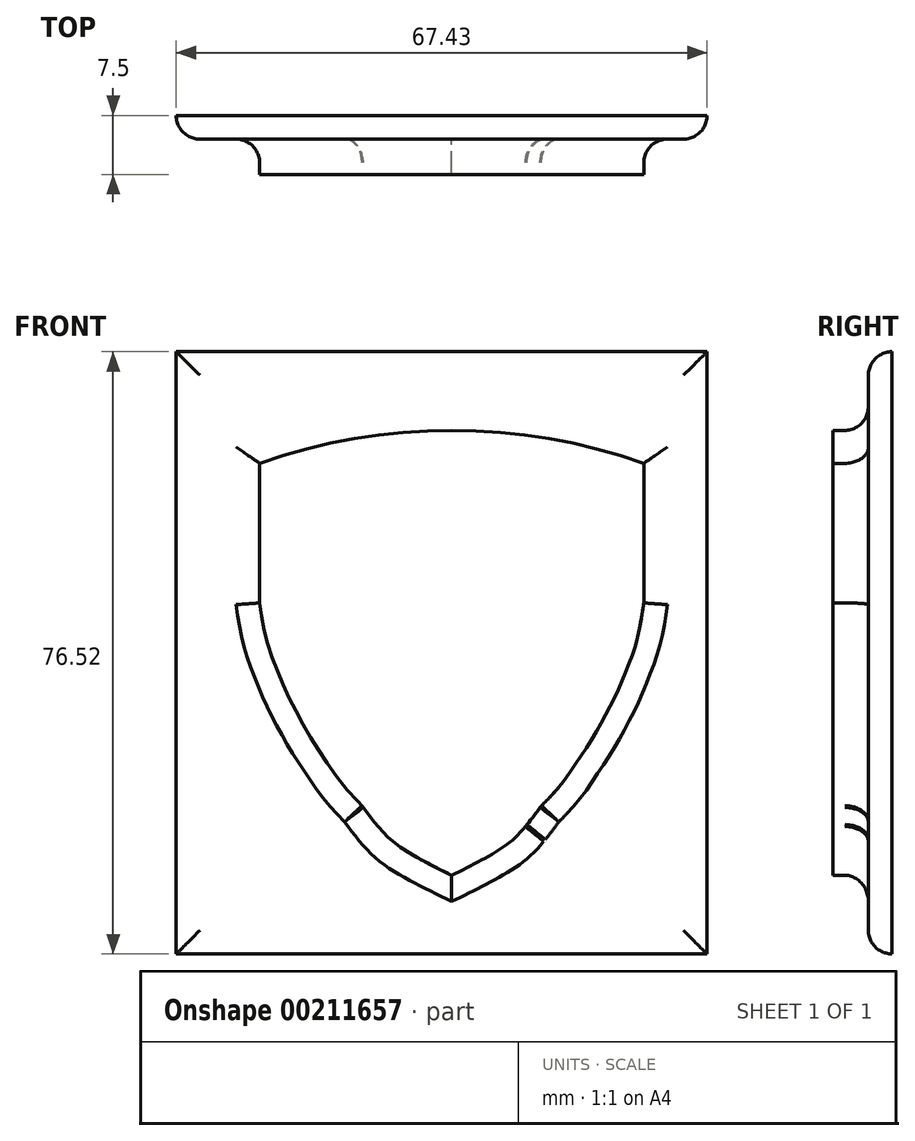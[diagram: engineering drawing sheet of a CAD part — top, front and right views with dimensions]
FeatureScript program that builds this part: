
annotation { "Feature Type Name" : "Feature", "Feature Type Description" : "" }
export const myFeature = defineFeature(function(context is Context, id is Id, definition is map)
    precondition{}
    {
        {
            var Q0;
            Q0=qCreatedBy(makeId("Front.planeOp"),FACE);
            var sketch = newSketch(context, id + "F0", { "sketchPlane" : qUnion([Q0])});
            skLineSegment(sketch, "E0", {"start": v(0, 9.74) * mm, "end": v(0, -11.29) * mm, "construction": true});
            skPoint(sketch, "E1", {"position": v(0, 0) * mm});
            skPoint(sketch, "E2", {"position": v(5.18, 2.71) * mm});
            skPoint(sketch, "E3", {"position": v(8.7, 5.42) * mm});
            skPoint(sketch, "E4", {"position": v(11.31, 8.72) * mm});
            skPoint(sketch, "E5", {"position": v(13.8, 11.44) * mm});
            skPoint(sketch, "E6", {"position": v(16.12, 14.74) * mm});
            skPoint(sketch, "E7", {"position": v(17.92, 17.5) * mm});
            skPoint(sketch, "E8", {"position": v(19.54, 20.38) * mm});
            skPoint(sketch, "E9", {"position": v(21.02, 23.3) * mm});
            skPoint(sketch, "E10", {"position": v(22.2, 26.15) * mm});
            skPoint(sketch, "E11", {"position": v(23.32, 29.13) * mm});
            skLineSegment(sketch, "E12", {"start": v(24.55, 35.46) * mm, "end": v(24.55, 33.78) * mm, "construction": true});
            skPoint(sketch, "E13", {"position": v(23.97, 31.94) * mm});
            skPoint(sketch, "E14", {"position": v(24.55, 34.6) * mm});
            skLineSegment(sketch, "E15", {"start": v(24.4, 53.9) * mm, "end": v(24.4, 50.6) * mm, "construction": true});
            skPoint(sketch, "E15.startSnap0", {"position": v(24.4, 52.32) * mm});
            skLineSegment(sketch, "E16", {"start": v(24.4, 40.4) * mm, "end": v(24.4, 36.95) * mm, "construction": true});
            skPoint(sketch, "E17", {"position": v(24.4, 37.61) * mm});
            skLineSegment(sketch, "E18", {"start": v(24.4, 52.32) * mm, "end": v(24.4, 37.61) * mm});
            skLineSegment(sketch, "E19", {"start": v(24.4, 38.33) * mm, "end": v(24.4, 34.6) * mm});
            skFitSpline(sketch, "E20", {"points": [v(24.4, 34.6) * mm, v(23.97, 31.94) * mm, v(23.32, 29.13) * mm, v(22.2, 26.15) * mm, v(21.02, 23.3) * mm, v(19.54, 20.38) * mm, v(17.92, 17.5) * mm, v(16.12, 14.74) * mm, v(13.8, 11.44) * mm, v(11.65, 9.07) * mm, v(11.36, 8.78) * mm, v(11.36, 8.78) * mm, v(11.31, 8.72) * mm, v(11.13, 8.48) * mm, v(8.7, 5.42) * mm, v(5.18, 2.71) * mm, v(0, 0) * mm], "startDerivative": vector(-5.52, -36.86) * mm, "endDerivative": vector(-51.25, -25.23) * mm});
            skLineSegment(sketch, "E21", {"start": v(12.42, 9.87) * mm, "end": v(9.37, 6.2) * mm});
            skLineSegment(sketch, "E22.MirrorCS", {"start": v(-24.4, 52.32) * mm, "end": v(-24.4, 37.61) * mm});
            skLineSegment(sketch, "E23.MirrorCS", {"start": v(-24.4, 38.33) * mm, "end": v(-24.4, 34.6) * mm});
            skFitSpline(sketch, "E24.MirrorCS", {"points": [v(-24.4, 34.6) * mm, v(-23.97, 31.94) * mm, v(-23.32, 29.13) * mm, v(-22.2, 26.15) * mm, v(-21.02, 23.3) * mm, v(-19.54, 20.38) * mm, v(-17.92, 17.5) * mm, v(-16.12, 14.74) * mm, v(-13.8, 11.44) * mm, v(-11.65, 9.07) * mm, v(-11.36, 8.78) * mm, v(-11.36, 8.78) * mm, v(-11.31, 8.72) * mm, v(-11.13, 8.48) * mm, v(-8.7, 5.42) * mm, v(-5.18, 2.71) * mm, v(0, 0) * mm], "startDerivative": vector(5.52, -36.86) * mm, "endDerivative": vector(51.25, -25.23) * mm});
            skLineSegment(sketch, "E25", {"start": v(0, 7.03) * mm, "end": v(0, 59.9) * mm, "construction": true});
            skLineSegment(sketch, "E26", {"start": v(-3.92, 56.52) * mm, "end": v(5.95, 56.52) * mm, "construction": true});
            skPoint(sketch, "E27", {"position": v(0, 56.52) * mm});
            skPoint(sketch, "E28", {"position": v(-24.4, 52.32) * mm});
            skPoint(sketch, "E29", {"position": v(24.4, 53.9) * mm});
            skArc(sketch, "E30", {"start": v(24.4, 52.32) * mm, "mid": v(0, 56.52) * mm, "end": v(-24.4, 52.32) * mm});
            skSolve(sketch);
        }
        {
            var Q0;
            {var subQ9=sQuery(id+"F0.wireOp",EDGE,"E18");Q0=makeQuery(id+"F0.imprint","IMPRINT",FACE,{"disambiguationData":[TD([[makeQuery(id+"F0.imprint","IMPRINT",EDGE,{"derivedFrom":subQ9}),-1.0]])]});}
            extrude(context, id + "F1", {"entities" : qUnion([Q0]), "depth" : 4.5 * mm});
        }
        {
            var Q0;
            Q0=qCreatedBy(makeId("Front.planeOp"),FACE);
            var sketch = newSketch(context, id + "F2", { "sketchPlane" : qUnion([Q0])});
            skLineSegment(sketch, "E31", {"start": v(-35, 66.52) * mm, "end": v(-35, -10) * mm});
            skLineSegment(sketch, "E32", {"start": v(32.43, 66.52) * mm, "end": v(32.43, -10) * mm});
            skLineSegment(sketch, "E33", {"start": v(-35, 66.52) * mm, "end": v(32.43, 66.52) * mm});
            skLineSegment(sketch, "E34", {"start": v(-35, -10) * mm, "end": v(32.43, -10) * mm});
            skSolve(sketch);
        }
        {
            var Q0;
            Q0 = qSketchRegion(id + "F2", true);
            var Q1;
            Q1=makeQuery(id+"F1.opExtrude","CAP_FACE",FACE,{"disambiguationData":[OSD([sQuery(id+"F0.wireOp",EDGE,"E18"),sQuery(id+"F0.wireOp",EDGE,"E19"),sQuery(id+"F0.wireOp",EDGE,"E20"),sQuery(id+"F0.wireOp",EDGE,"E21"),sQuery(id+"F0.wireOp",EDGE,"E22.MirrorCS"),sQuery(id+"F0.wireOp",EDGE,"E23.MirrorCS"),sQuery(id+"F0.wireOp",EDGE,"E24.MirrorCS"),sQuery(id+"F0.wireOp",EDGE,"E30")])],"isStart":false});
            extrude(context, id + "F3", {"entities" : qUnion([Q0, Q1]), "operationType" : NewBodyOperationType.ADD, "depth" : 3 * mm});
        }
        {
            var Q0;
            Q0=makeQuery(id+"F3.opExtrude","CAP_EDGE",EDGE,{"disambiguationData":[OSD([sQuery(id+"F2.wireOp",EDGE,"E33")])],"isStart":false});
            var Q1;
            Q1=makeQuery(id+"F3.opExtrude","CAP_EDGE",EDGE,{"disambiguationData":[OSD([sQuery(id+"F2.wireOp",EDGE,"E31")])],"isStart":false});
            var Q2;
            Q2=makeQuery(id+"F3.opExtrude","CAP_EDGE",EDGE,{"disambiguationData":[OSD([sQuery(id+"F2.wireOp",EDGE,"E32")])],"isStart":false});
            var Q3;
            Q3=makeQuery(id+"F3.opExtrude","CAP_EDGE",EDGE,{"disambiguationData":[OSD([sQuery(id+"F2.wireOp",EDGE,"E34")])],"isStart":false});
            fillet(context, id + "F4", {"entities" : qUnion([Q0, Q1, Q2, Q3]), "radius" : 3 * mm, "tangentPropagation" : true, "allowEdgeOverflow" : false});
        }
        {
            var Q0;
            {var subQ0=sQuery(id+"F0.wireOp",EDGE,"E21");var subQ1=sQuery(id+"F0.wireOp",EDGE,"E20");var subQ2=makeQuery(id+"F0.imprint","INTERSECT",VERTEX,{"disambiguationData":[OD(0.0)],"derivedFrom":[subQ1,subQ0]});Q0=makeQuery(id+"F3.boolean.opBoolean","INTERSECT",EDGE,{"derivedFrom":[makeQuery(id+"F3.opExtrude","SWEPT_FACE",FACE,{"disambiguationData":[OSD([subQ1]),TDD([makeQuery(id+"F1.opExtrude","CAP_EDGE",EDGE,{"disambiguationData":[OSD([subQ1]),TDD([makeQuery(id+"F0.imprint","IMPRINT",EDGE,{"disambiguationData":[TD([[makeQuery(id+"F0.imprint","INTERSECT",VERTEX,{"derivedFrom":[sQuery(id+"F0.wireOp",EDGE,"E19"),subQ1]}),-1.0]])],"derivedFrom":subQ1}),makeQuery(id+"F0.imprint","IMPRINT",EDGE,{"disambiguationData":[TD([[subQ2,-1.0]])],"derivedFrom":subQ1})])],"isStart":false})])]}),makeQuery(id+"F3.opExtrude","CAP_FACE",FACE,{"disambiguationData":[OSD([sQuery(id+"F2.wireOp",EDGE,"E31"),sQuery(id+"F2.wireOp",EDGE,"E32"),sQuery(id+"F2.wireOp",EDGE,"E33"),sQuery(id+"F2.wireOp",EDGE,"E34")])],"isStart":false})]});}
            fillet(context, id + "F5", {"entities" : qUnion([Q0]), "radius" : 3 * mm, "tangentPropagation" : true, "allowEdgeOverflow" : false});
        }
        {
            var Q0;
            Q0=makeQuery(id+"F3.boolean.opBoolean","INTERSECT",EDGE,{"derivedFrom":[makeQuery(id+"F3.opExtrude","SWEPT_FACE",FACE,{"disambiguationData":[OSD([sQuery(id+"F0.wireOp",EDGE,"E18"),sQuery(id+"F0.wireOp",EDGE,"E19")])]}),makeQuery(id+"F3.opExtrude","CAP_FACE",FACE,{"disambiguationData":[OSD([sQuery(id+"F2.wireOp",EDGE,"E31"),sQuery(id+"F2.wireOp",EDGE,"E32"),sQuery(id+"F2.wireOp",EDGE,"E33"),sQuery(id+"F2.wireOp",EDGE,"E34")])],"isStart":false})]});
            fillet(context, id + "F6", {"entities" : qUnion([Q0]), "radius" : 3 * mm, "tangentPropagation" : true, "allowEdgeOverflow" : false});
        }
        {
            var Q0;
            Q0=makeQuery(id+"F3.boolean.opBoolean","INTERSECT",EDGE,{"derivedFrom":[makeQuery(id+"F3.opExtrude","SWEPT_FACE",FACE,{"disambiguationData":[OSD([sQuery(id+"F0.wireOp",EDGE,"E30")])]}),makeQuery(id+"F3.opExtrude","CAP_FACE",FACE,{"disambiguationData":[OSD([sQuery(id+"F2.wireOp",EDGE,"E31"),sQuery(id+"F2.wireOp",EDGE,"E32"),sQuery(id+"F2.wireOp",EDGE,"E33"),sQuery(id+"F2.wireOp",EDGE,"E34")])],"isStart":false})]});
            fillet(context, id + "F7", {"entities" : qUnion([Q0]), "radius" : 3 * mm, "tangentPropagation" : true, "allowEdgeOverflow" : false});
        }
        {
            var Q0;
            Q0=makeQuery(id+"F3.boolean.opBoolean","INTERSECT",EDGE,{"derivedFrom":[makeQuery(id+"F3.opExtrude","SWEPT_FACE",FACE,{"disambiguationData":[OSD([sQuery(id+"F0.wireOp",EDGE,"E24.MirrorCS")])]}),makeQuery(id+"F3.opExtrude","CAP_FACE",FACE,{"disambiguationData":[OSD([sQuery(id+"F2.wireOp",EDGE,"E31"),sQuery(id+"F2.wireOp",EDGE,"E32"),sQuery(id+"F2.wireOp",EDGE,"E33"),sQuery(id+"F2.wireOp",EDGE,"E34")])],"isStart":false})]});
            fillet(context, id + "F8", {"entities" : qUnion([Q0]), "radius" : 3 * mm, "tangentPropagation" : true, "allowEdgeOverflow" : false});
        }
        {
            var Q0;
            Q0=makeQuery(id+"F3.boolean.opBoolean","INTERSECT",EDGE,{"derivedFrom":[makeQuery(id+"F3.opExtrude","SWEPT_FACE",FACE,{"disambiguationData":[OSD([sQuery(id+"F0.wireOp",EDGE,"E22.MirrorCS"),sQuery(id+"F0.wireOp",EDGE,"E23.MirrorCS")])]}),makeQuery(id+"F3.opExtrude","CAP_FACE",FACE,{"disambiguationData":[OSD([sQuery(id+"F2.wireOp",EDGE,"E31"),sQuery(id+"F2.wireOp",EDGE,"E32"),sQuery(id+"F2.wireOp",EDGE,"E33"),sQuery(id+"F2.wireOp",EDGE,"E34")])],"isStart":false})]});
            fillet(context, id + "F9", {"entities" : qUnion([Q0]), "radius" : 3 * mm, "tangentPropagation" : true, "allowEdgeOverflow" : false});
        }
    });
